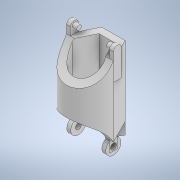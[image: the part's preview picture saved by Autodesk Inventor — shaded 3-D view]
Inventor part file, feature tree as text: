
AUTODESK INVENTOR PART (.ipt)
format: ipt  version: 2022 (Build 260153000, 153)  size: 280,576 bytes
history: native  units: mm
features: extrude x15, sketch x11, other x2, shell x1, projected_geometry x1
ambient origin geometry x8: Origin, YZ Plane, XZ Plane, XY Plane, X Axis, Y Axis, Z Axis, Center Point
bodies: Body1 (feature_tree)
feature tree (30):
  other  "솔리드1"
  sketch  "스케치1"
  extrude  "돌출1"  Depth=20.0mm
  sketch  "스케치7"
  extrude  "돌출7"  Depth=10.0mm
  shell  "쉘2"  Thickness=5.0mm
  extrude  "돌출8"  Depth=30.0mm TaperAngle=0.0deg
  extrude  "돌출9"  Depth=9.0mm
  sketch  "스케치9"
  extrude  "돌출10"  Depth=30.0mm TaperAngle=0.0deg
  sketch  "스케치11"
  sketch  "스케치13"
  sketch  "스케치14"
  extrude  "돌출12"  Depth=3.0mm
  extrude  "돌출13"  Depth=30.0mm TaperAngle=0.0deg
  sketch  "스케치15"
  extrude  "돌출14"  Depth=5.0mm TaperAngle=0.0deg
  extrude  "돌출15"  Depth=5.0mm TaperAngle=0.0deg
  extrude  "돌출16"  Depth=2.0mm
  extrude  "돌출17"  Depth=2.5mm
  other  "작업 평면1"
  extrude  "돌출19"  Depth=8.0mm TaperAngle=0.0deg
  extrude  "돌출20"  Depth=8.0mm TaperAngle=0.0deg
  extrude  "돌출21"  Depth=100.0mm TaperAngle=0.0deg
  extrude  "돌출22"  Depth=2.0mm TaperAngle=0.0deg
  sketch  "스케치8"
  sketch  "스케치10"
  projected_geometry  "투영된 루프1"
  sketch  "스케치16"
  sketch  "스케치18"
